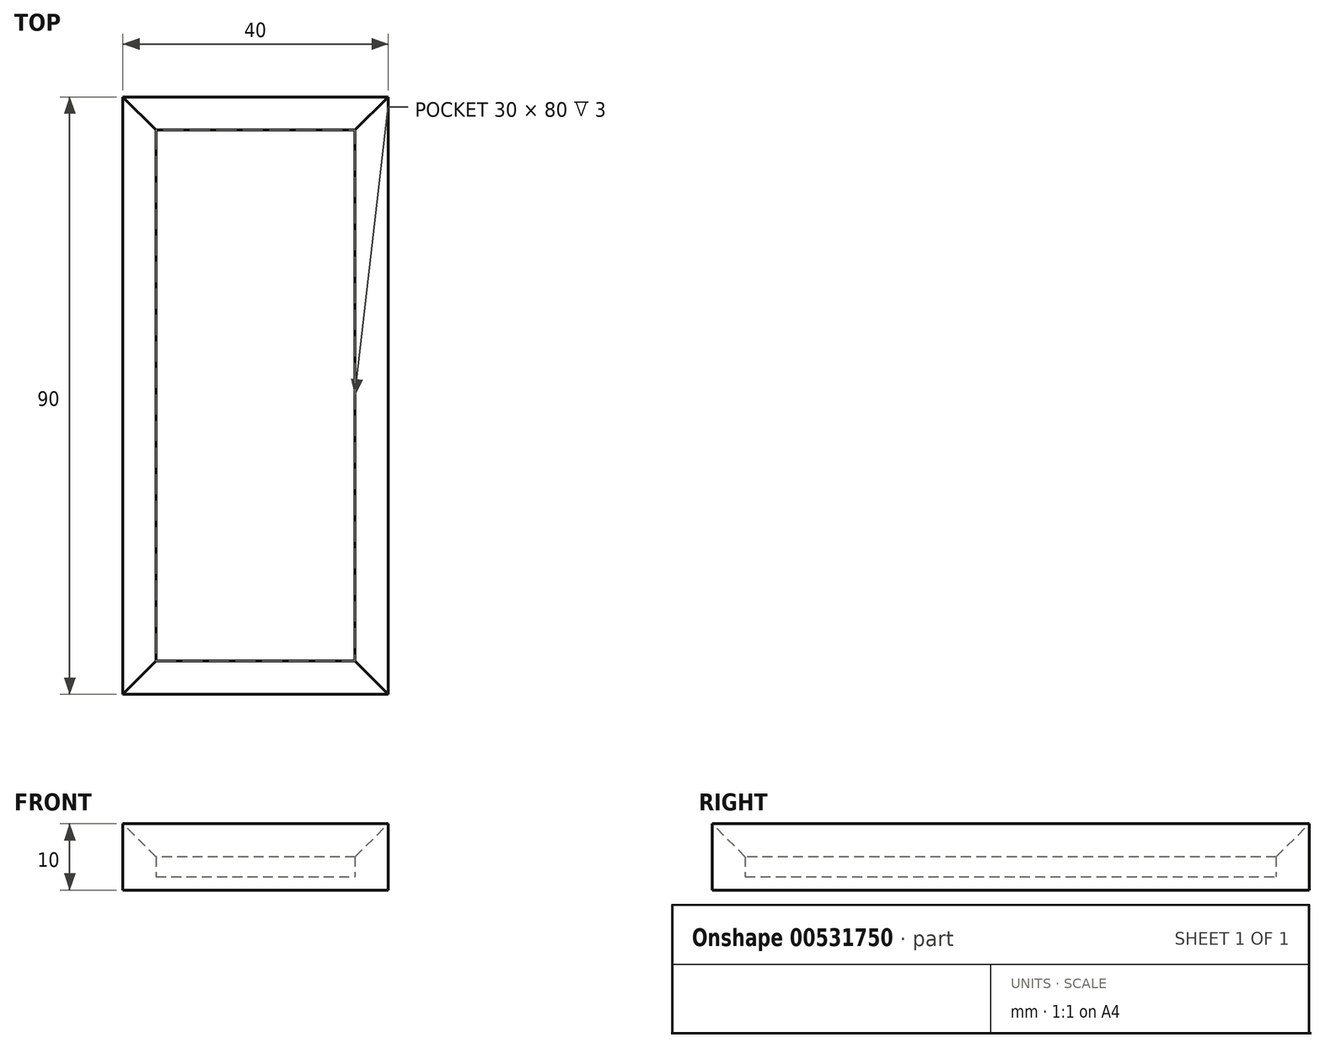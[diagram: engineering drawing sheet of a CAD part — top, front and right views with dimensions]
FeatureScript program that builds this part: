
annotation { "Feature Type Name" : "Feature", "Feature Type Description" : "" }
export const myFeature = defineFeature(function(context is Context, id is Id, definition is map)
    precondition{}
    {
        {
            var Q0;
            Q0=qCreatedBy(makeId("Top.planeOp"),FACE);
            var sketch = newSketch(context, id + "F0", { "sketchPlane" : qUnion([Q0])});
            skLineSegment(sketch, "E0.bottom", {"start": v(-18.57, 82.22) * mm, "end": v(21.43, 82.22) * mm});
            skLineSegment(sketch, "E0.top", {"start": v(-18.57, -7.78) * mm, "end": v(21.43, -7.78) * mm});
            skLineSegment(sketch, "E0.left", {"start": v(-18.57, 82.22) * mm, "end": v(-18.57, -7.78) * mm});
            skLineSegment(sketch, "E0.right", {"start": v(21.43, 82.22) * mm, "end": v(21.43, -7.78) * mm});
            skLineSegment(sketch, "E1", {"start": v(-13.57, 77.22) * mm, "end": v(16.43, 77.22) * mm});
            skLineSegment(sketch, "E2", {"start": v(16.43, 77.22) * mm, "end": v(16.43, -2.78) * mm});
            skLineSegment(sketch, "E3", {"start": v(16.43, -2.78) * mm, "end": v(-13.57, -2.78) * mm});
            skLineSegment(sketch, "E4", {"start": v(-13.57, -2.78) * mm, "end": v(-13.57, 77.22) * mm});
            skSolve(sketch);
        }
        {
            var Q0;
            Q0=makeQuery(id+"F0.imprint","IMPRINT",FACE,{"disambiguationData":[TD([[makeQuery(id+"F0.imprint","IMPRINT",EDGE,{"derivedFrom":sQuery(id+"F0.wireOp",EDGE,"E0.bottom")}),-1.0]])]});
            var Q1;
            Q1=sQuery(id+"F0.wireOp",EDGE,"E0.right");
            var Q2;
            Q2=sQuery(id+"F0.wireOp",EDGE,"E0.bottom");
            var Q3;
            Q3=sQuery(id+"F0.wireOp",EDGE,"E0.left");
            var Q4;
            Q4=sQuery(id+"F0.wireOp",EDGE,"E0.top");
            var Q5;
            Q5=sQuery(id+"F0.wireOp",EDGE,"E2");
            var Q6;
            Q6=sQuery(id+"F0.wireOp",EDGE,"E3");
            var Q7;
            Q7=sQuery(id+"F0.wireOp",EDGE,"E4");
            var Q8;
            Q8=sQuery(id+"F0.wireOp",EDGE,"E1");
            extrude(context, id + "F1", {"entities" : qUnion([Q0]), "surfaceEntities" : qUnion([Q1, Q2, Q3, Q4, Q5, Q6, Q7, Q8]), "depth" : 10 * mm, "offsetDistance" : 25 * mm});
        }
        {
            var Q0;
            Q0=makeQuery(id+"F0.imprint","IMPRINT",FACE,{"disambiguationData":[TD([[makeQuery(id+"F0.imprint","IMPRINT",EDGE,{"derivedFrom":sQuery(id+"F0.wireOp",EDGE,"E1")}),-1.0]])]});
            extrude(context, id + "F2", {"entities" : qUnion([Q0]), "operationType" : NewBodyOperationType.ADD, "depth" : 2 * mm, "offsetDistance" : 25 * mm});
        }
        {
            var Q0;
            Q0=makeQuery(id+"F1.opExtrude","CAP_EDGE",EDGE,{"disambiguationData":[OSD([sQuery(id+"F0.wireOp",EDGE,"E2")])],"isStart":false});
            var Q1;
            Q1=makeQuery(id+"F1.opExtrude","CAP_EDGE",EDGE,{"disambiguationData":[OSD([sQuery(id+"F0.wireOp",EDGE,"E1")])],"isStart":false});
            var Q2;
            Q2=makeQuery(id+"F1.opExtrude","CAP_EDGE",EDGE,{"disambiguationData":[OSD([sQuery(id+"F0.wireOp",EDGE,"E4")])],"isStart":false});
            var Q3;
            Q3=makeQuery(id+"F1.opExtrude","CAP_EDGE",EDGE,{"disambiguationData":[OSD([sQuery(id+"F0.wireOp",EDGE,"E3")])],"isStart":false});
            chamfer(context, id + "F3", {"entities" : qUnion([Q0, Q1, Q2, Q3]), "width" : 5 * mm, "tangentPropagation" : true});
        }
    });
